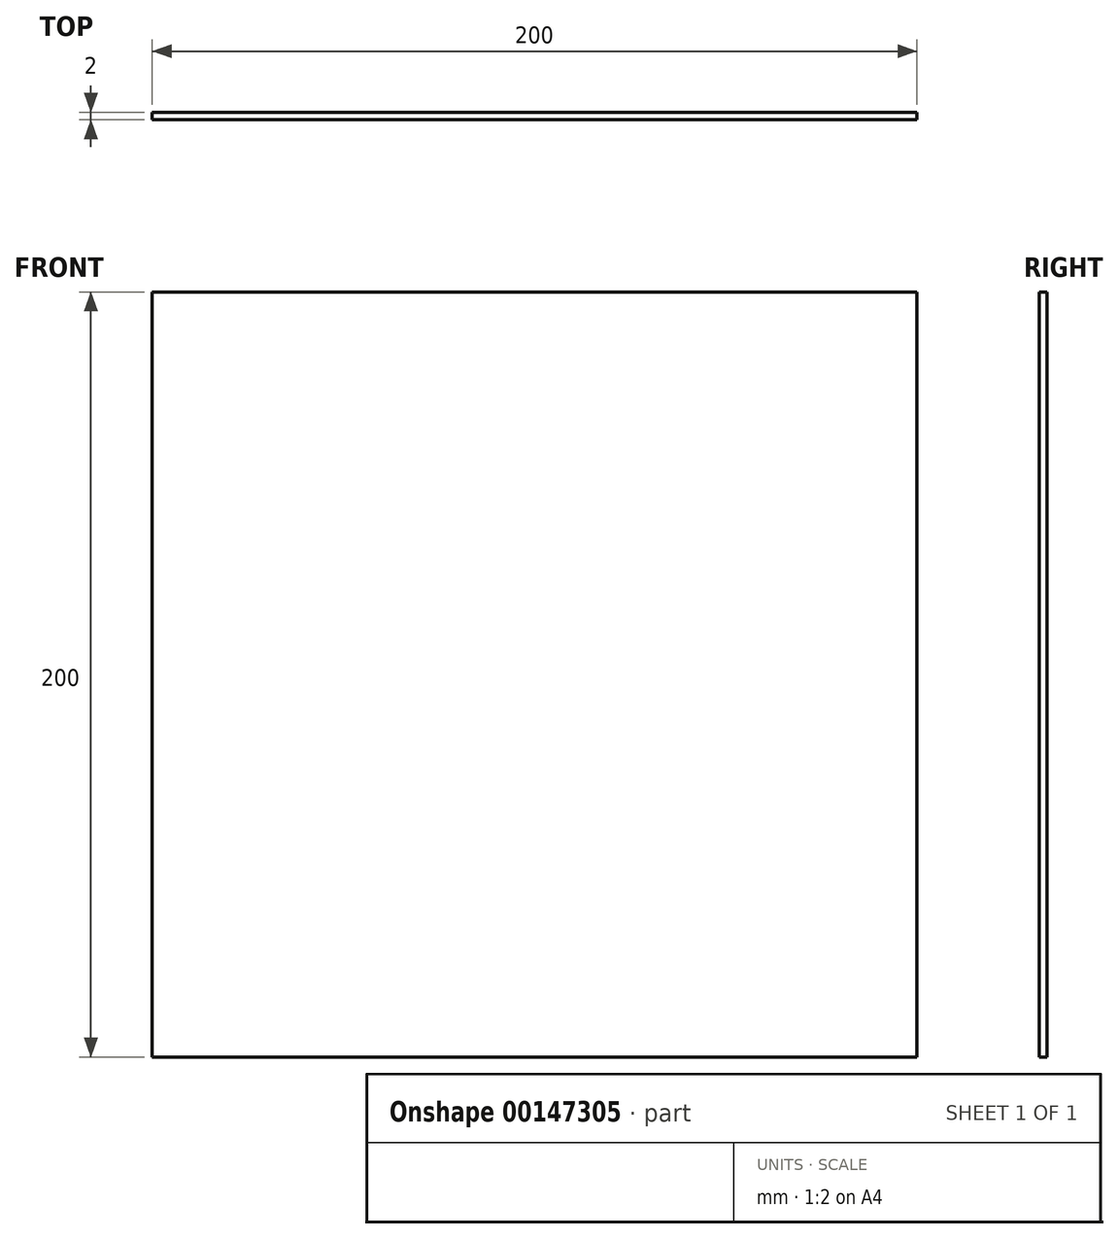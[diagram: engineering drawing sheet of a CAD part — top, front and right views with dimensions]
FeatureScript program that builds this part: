
annotation { "Feature Type Name" : "Feature", "Feature Type Description" : "" }
export const myFeature = defineFeature(function(context is Context, id is Id, definition is map)
    precondition{}
    {
        {
            var Q0;
            Q0=qCreatedBy(makeId("Front.planeOp"),FACE);
            var sketch = newSketch(context, id + "F0", { "sketchPlane" : qUnion([Q0])});
            skLineSegment(sketch, "E0.bottom", {"start": v(100, 100) * mm, "end": v(-100, 100) * mm});
            skLineSegment(sketch, "E0.top", {"start": v(100, -100) * mm, "end": v(-100, -100) * mm});
            skLineSegment(sketch, "E0.left", {"start": v(100, 100) * mm, "end": v(100, -100) * mm});
            skLineSegment(sketch, "E0.right", {"start": v(-100, 100) * mm, "end": v(-100, -100) * mm});
            skPoint(sketch, "E0.middle", {"position": v(0, 0) * mm});
            skSolve(sketch);
        }
        {
            var Q0;
            Q0=makeQuery(id+"F0.imprint","IMPRINT",FACE,{"disambiguationData":[TD([[makeQuery(id+"F0.imprint","IMPRINT",EDGE,{"derivedFrom":sQuery(id+"F0.wireOp",EDGE,"E0.bottom")}),1.0]])]});
            extrude(context, id + "F1", {"entities" : qUnion([Q0]), "depth" : 2 * mm});
        }
    });
